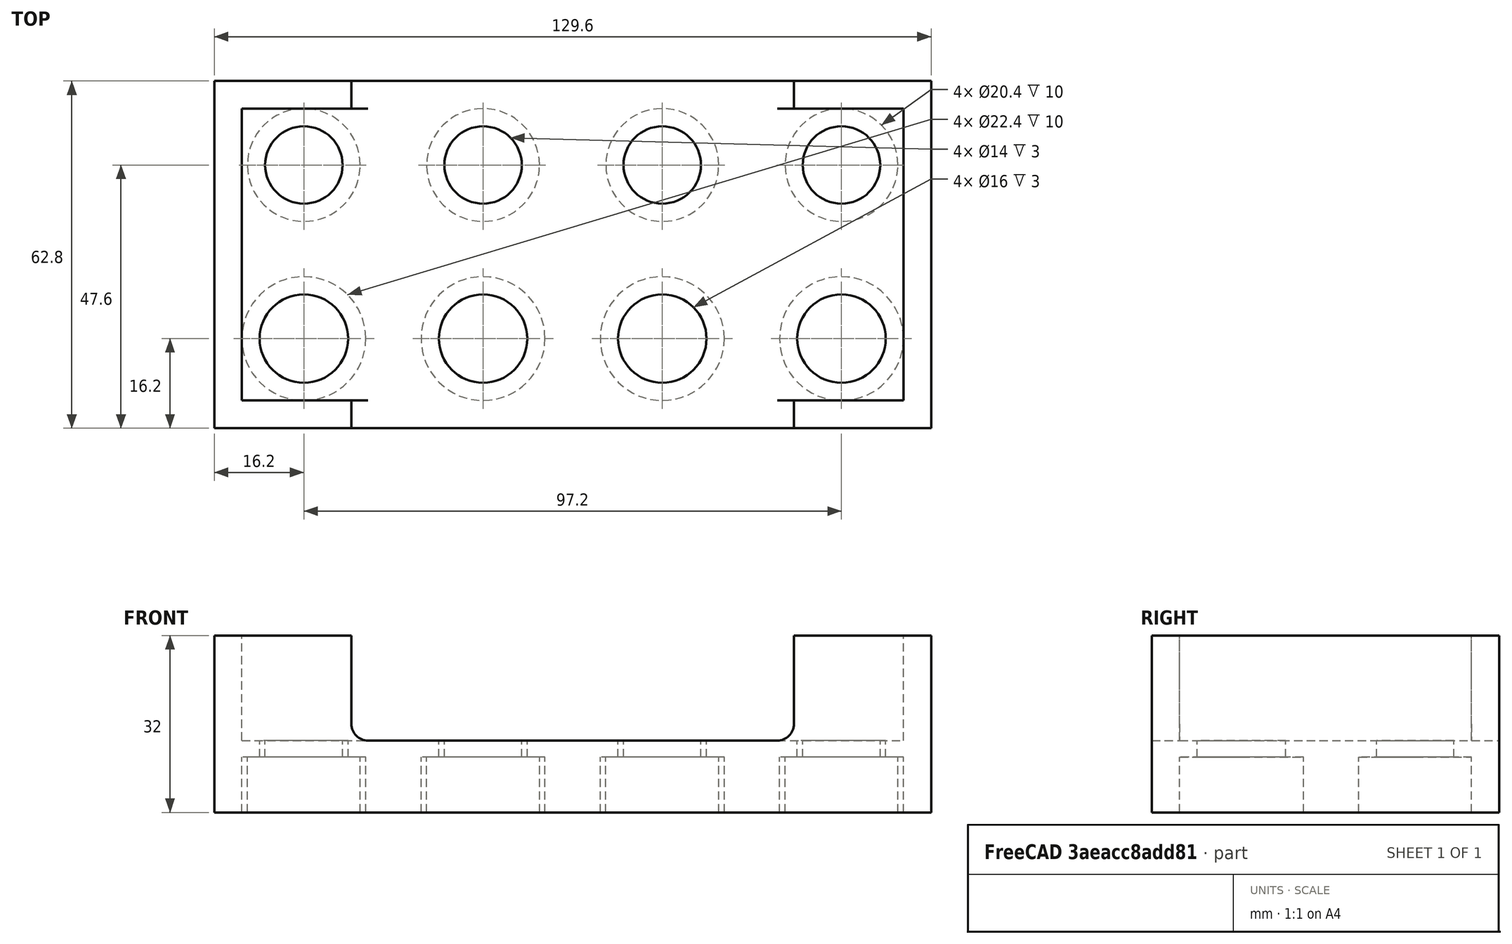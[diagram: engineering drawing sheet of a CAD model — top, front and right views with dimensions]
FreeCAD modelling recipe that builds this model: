
FCSTD DOCUMENT  (FreeCAD 0.18R16110 (Git))
Label: vial-6-8-rack
License: All rights reserved
LicenseURL: http://en.wikipedia.org/wiki/All_rights_reserved
objects: Part::Cut×19, Part::Cylinder×16, Part::Box×5, Part::Fillet×2, Part::MultiFuse×1, Mesh::Feature×1
note: 43 computed .brp shape members not serialized (recipe doc carries the construction recipe); baked Part::Feature solids carry a one-line shape summary decoded from their .brp

FEATURE [Part::Cylinder] Cylinder  label="Zylinder"
  Angle = 360
  AttacherType = Attacher::AttachEngine3D
  Height = 10
  Radius = 11.2
  expr: Radius = 22.4 / 2
FEATURE [Part::Cylinder] Cylinder001  label="Zylinder001"
  Angle = 360
  AttacherType = Attacher::AttachEngine3D
  Height = 10
  Placement = pos=(32.4,0,0) rot=(0,0,1;0rad)
  Radius = 11.2
  expr: Placement.Base.x = 22.4 + 10
  expr: Radius = 22.4 / 2
FEATURE [Part::Cylinder] Cylinder002  label="Zylinder002"
  Angle = 360
  AttacherType = Attacher::AttachEngine3D
  Height = 10
  Placement = pos=(64.8,0,0) rot=(0,0,1;0rad)
  Radius = 11.2
  expr: Placement.Base.x = (22.4 + 10) * 2
  expr: Radius = 22.4 / 2
FEATURE [Part::Cylinder] Cylinder003  label="Zylinder003"
  Angle = 360
  AttacherType = Attacher::AttachEngine3D
  Height = 10
  Placement = pos=(97.2,0,0) rot=(0,0,1;0rad)
  Radius = 11.2
  expr: Placement.Base.x = (22.4 + 10) * 3
  expr: Radius = 22.4 / 2
FEATURE [Part::Cylinder] Cylinder004  label="Zylinder004"
  Angle = 360
  AttacherType = Attacher::AttachEngine3D
  Height = 10
  Placement = pos=(0,31.4,0) rot=(0,0,1;0rad)
  Radius = 10.2
  expr: Placement.Base.y = 22.4 / 2 + 20.4 / 2 + 10
  expr: Radius = 20.4 / 2
FEATURE [Part::Cylinder] Cylinder005  label="Zylinder005"
  Angle = 360
  AttacherType = Attacher::AttachEngine3D
  Height = 10
  Placement = pos=(64.8,31.4,0) rot=(0,0,1;0rad)
  Radius = 10.2
  expr: Placement.Base.x = (22.4 + 10) * 2
  expr: Placement.Base.y = 22.4 / 2 + 20.4 / 2 + 10
  expr: Radius = 20.4 / 2
FEATURE [Part::Cylinder] Cylinder006  label="Zylinder006"
  Angle = 360
  AttacherType = Attacher::AttachEngine3D
  Height = 10
  Placement = pos=(32.4,31.4,0) rot=(0,0,1;0rad)
  Radius = 10.2
  expr: Placement.Base.x = 22.4 + 10
  expr: Placement.Base.y = 22.4 / 2 + 20.4 / 2 + 10
  expr: Radius = 20.4 / 2
FEATURE [Part::Cylinder] Cylinder007  label="Zylinder007"
  Angle = 360
  AttacherType = Attacher::AttachEngine3D
  Height = 10
  Placement = pos=(97.2,31.4,0) rot=(0,0,1;0rad)
  Radius = 10.2
  expr: Placement.Base.x = (22.4 + 10) * 3
  expr: Placement.Base.y = 22.4 / 2 + 20.4 / 2 + 10
  expr: Radius = 20.4 / 2
FEATURE [Part::Box] Box  label="Quader"
  AttacherType = Attacher::AttachEngine3D
  Height = 13
  Length = 129.6
  Placement = pos=(-16.2,-16.2,0) rot=(0,0,1;0rad)
  Width = 62.8
  expr: Placement.Base.y = -22.4 / 2 - 5
  expr: Placement.Base.x = -22.4 / 2 - 5
FEATURE [Part::Cut] Cut
  Base = -> Box
  Tool = -> Cylinder007
FEATURE [Part::Cut] Cut001
  Base = -> Cut
  Tool = -> Cylinder006
FEATURE [Part::Cut] Cut002
  Base = -> Cut001
  Tool = -> Cylinder005
FEATURE [Part::Cut] Cut003
  Base = -> Cut002
  Tool = -> Cylinder004
FEATURE [Part::Cut] Cut004
  Base = -> Cut003
  Tool = -> Cylinder003
FEATURE [Part::Cut] Cut005
  Base = -> Cut004
  Tool = -> Cylinder002
FEATURE [Part::Cut] Cut006
  Base = -> Cut005
  Tool = -> Cylinder001
FEATURE [Part::Cut] Cut007
  Base = -> Cut006
  Tool = -> Cylinder
FEATURE [Part::Box] Box001  label="Quader001"
  AttacherType = Attacher::AttachEngine3D
  Height = 19
  Length = 129.6
  Placement = pos=(-16.2,-16.2,13) rot=(0,0,1;0rad)
  Width = 62.8
  expr: Placement.Base.y = -22.4 / 2 - 5
  expr: Placement.Base.x = -22.4 / 2 - 5
FEATURE [Part::Box] Box002  label="Quader002"
  AttacherType = Attacher::AttachEngine3D
  Height = 19
  Length = 119.6
  Placement = pos=(-11.2,-11.2,13) rot=(0,0,1;0rad)
  Width = 52.8
  expr: Placement.Base.y = -22.4 / 2
  expr: Placement.Base.x = -22.4 / 2
FEATURE [Part::Cut] Cut008
  Base = -> Box001
  Tool = -> Box002
FEATURE [Part::MultiFuse] Fusion
  Shapes = -> [Cut007,Cut008]
FEATURE [Part::Cylinder] Cylinder008  label="Zylinder008"
  Angle = 360
  AttacherType = Attacher::AttachEngine3D
  Height = 18
  Radius = 8
FEATURE [Part::Cylinder] Cylinder009  label="Zylinder009"
  Angle = 360
  AttacherType = Attacher::AttachEngine3D
  Height = 18
  Placement = pos=(32.4,0,0) rot=(0,0,1;0rad)
  Radius = 8
  expr: Placement.Base.x = 32.4
FEATURE [Part::Cylinder] Cylinder010  label="Zylinder010"
  Angle = 360
  AttacherType = Attacher::AttachEngine3D
  Height = 18
  Placement = pos=(64.8,0,0) rot=(0,0,1;0rad)
  Radius = 8
  expr: Placement.Base.x = 32.4 * 2
FEATURE [Part::Cylinder] Cylinder011  label="Zylinder011"
  Angle = 360
  AttacherType = Attacher::AttachEngine3D
  Height = 18
  Placement = pos=(97.2,0,0) rot=(0,0,1;0rad)
  Radius = 8
  expr: Placement.Base.x = 32.4 * 3
FEATURE [Part::Cylinder] Cylinder012  label="Zylinder012"
  Angle = 360
  AttacherType = Attacher::AttachEngine3D
  Height = 18
  Placement = pos=(97.2,31.4,0) rot=(0,0,1;0rad)
  Radius = 7
  expr: Placement.Base.x = 32.4 * 3
FEATURE [Part::Cylinder] Cylinder013  label="Zylinder013"
  Angle = 360
  AttacherType = Attacher::AttachEngine3D
  Height = 18
  Placement = pos=(64.8,31.4,0) rot=(0,0,1;0rad)
  Radius = 7
  expr: Placement.Base.x = 32.4 * 2
FEATURE [Part::Cylinder] Cylinder014  label="Zylinder014"
  Angle = 360
  AttacherType = Attacher::AttachEngine3D
  Height = 18
  Placement = pos=(32.4,31.4,0) rot=(0,0,1;0rad)
  Radius = 7
  expr: Placement.Base.x = 32.4
FEATURE [Part::Cylinder] Cylinder015  label="Zylinder015"
  Angle = 360
  AttacherType = Attacher::AttachEngine3D
  Height = 18
  Placement = pos=(0,31.4,0) rot=(0,0,1;0rad)
  Radius = 7
FEATURE [Part::Cut] Cut009
  Base = -> Fusion
  Tool = -> Cylinder008
FEATURE [Part::Cut] Cut010
  Base = -> Cut009
  Tool = -> Cylinder015
FEATURE [Part::Cut] Cut011
  Base = -> Cut010
  Tool = -> Cylinder014
FEATURE [Part::Cut] Cut012
  Base = -> Cut011
  Tool = -> Cylinder013
FEATURE [Part::Cut] Cut013
  Base = -> Cut012
  Tool = -> Cylinder012
FEATURE [Part::Cut] Cut014
  Base = -> Cut013
  Tool = -> Cylinder011
FEATURE [Part::Cut] Cut015
  Base = -> Cut014
  Tool = -> Cylinder010
FEATURE [Part::Cut] Cut016
  Base = -> Cut015
  Tool = -> Cylinder009
FEATURE [Part::Box] Box003  label="Quader003"
  AttacherType = Attacher::AttachEngine3D
  Height = 19
  Length = 80
  Placement = pos=(8.6,-16.2,13) rot=(0,0,1;0rad)
  Width = 5
  expr: Placement.Base.y = -22.4 / 2 - 5
  expr: Placement.Base.x = -22.4 / 2 - 5 + 129.6 / 2 - 40
FEATURE [Part::Box] Box004  label="Quader004"
  AttacherType = Attacher::AttachEngine3D
  Height = 19
  Length = 80
  Placement = pos=(8.6,41.6,13) rot=(0,0,1;0rad)
  Width = 5
  expr: Placement.Base.y = -22.4 / 2 - 5 + 62.8 - 5
  expr: Placement.Base.x = -22.4 / 2 - 5 + 129.6 / 2 - 40
FEATURE [Part::Fillet] Fillet
  Base = -> Box003
  Edges = 2 edges r=3: [Edge4,Edge8]
FEATURE [Part::Fillet] Fillet001
  Base = -> Box004
  Edges = 2 edges r=3: [Edge4,Edge8]
FEATURE [Part::Cut] Cut017
  Base = -> Cut016
  Tool = -> Fillet
FEATURE [Part::Cut] Cut018  label="vial-6-8-rack"
  Base = -> Cut017
  Tool = -> Fillet001
FEATURE [Mesh::Feature] Mesh  label="vial-6-8-rack(Meshed)"
